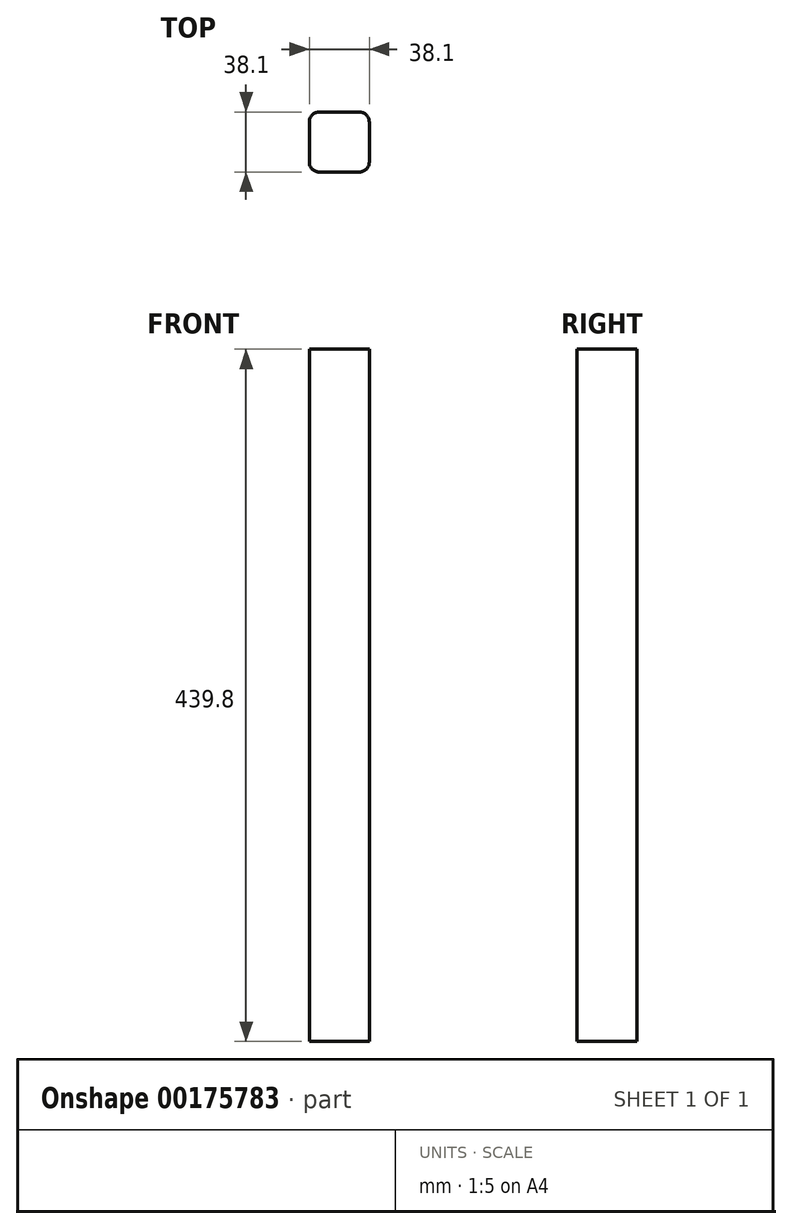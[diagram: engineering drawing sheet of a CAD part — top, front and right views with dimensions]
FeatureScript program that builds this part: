
annotation { "Feature Type Name" : "Feature", "Feature Type Description" : "" }
export const myFeature = defineFeature(function(context is Context, id is Id, definition is map)
    precondition{}
    {
        {
            var Q0;
            Q0=qCreatedBy(makeId("Top.planeOp"),FACE);
            var sketch = newSketch(context, id + "F0", { "sketchPlane" : qUnion([Q0])});
            skLineSegment(sketch, "E0.bottom", {"start": v(12.7, 19.05) * mm, "end": v(-12.7, 19.05) * mm});
            skLineSegment(sketch, "E0.top", {"start": v(12.7, -19.05) * mm, "end": v(-12.7, -19.05) * mm});
            skLineSegment(sketch, "E0.left", {"start": v(19.05, 12.7) * mm, "end": v(19.05, -12.7) * mm});
            skLineSegment(sketch, "E0.right", {"start": v(-19.05, 12.7) * mm, "end": v(-19.05, -12.7) * mm});
            skPoint(sketch, "E0.middle", {"position": v(0, 0) * mm});
            skPoint(sketch, "E1.visualSharp", {"position": v(-19.05, 19.05) * mm});
            skArc(sketch, "E1.filletArc", {"start": v(-12.7, 19.05) * mm, "mid": v(-17.2, 17.2) * mm, "end": v(-19.05, 12.7) * mm});
            skPoint(sketch, "E2.visualSharp", {"position": v(19.05, 19.05) * mm});
            skArc(sketch, "E2.filletArc", {"start": v(19.05, 12.7) * mm, "mid": v(17.2, 17.2) * mm, "end": v(12.7, 19.05) * mm});
            skPoint(sketch, "E3.visualSharp", {"position": v(19.05, -19.05) * mm});
            skArc(sketch, "E3.filletArc", {"start": v(12.7, -19.05) * mm, "mid": v(17.2, -17.2) * mm, "end": v(19.05, -12.7) * mm});
            skPoint(sketch, "E4.visualSharp", {"position": v(-19.05, -19.05) * mm});
            skArc(sketch, "E4.filletArc", {"start": v(-19.05, -12.7) * mm, "mid": v(-17.2, -17.2) * mm, "end": v(-12.7, -19.05) * mm});
            skSolve(sketch);
        }
        {
            var Q0;
            Q0=makeQuery(id+"F0.imprint","IMPRINT",FACE,{"disambiguationData":[TD([[makeQuery(id+"F0.imprint","IMPRINT",EDGE,{"derivedFrom":sQuery(id+"F0.wireOp",EDGE,"E0.bottom")}),1.0]])]});
            extrude(context, id + "F1", {"entities" : qUnion([Q0]), "depth" : 439.8 * mm, "offsetDistance" : 25.4 * mm});
        }
    });
